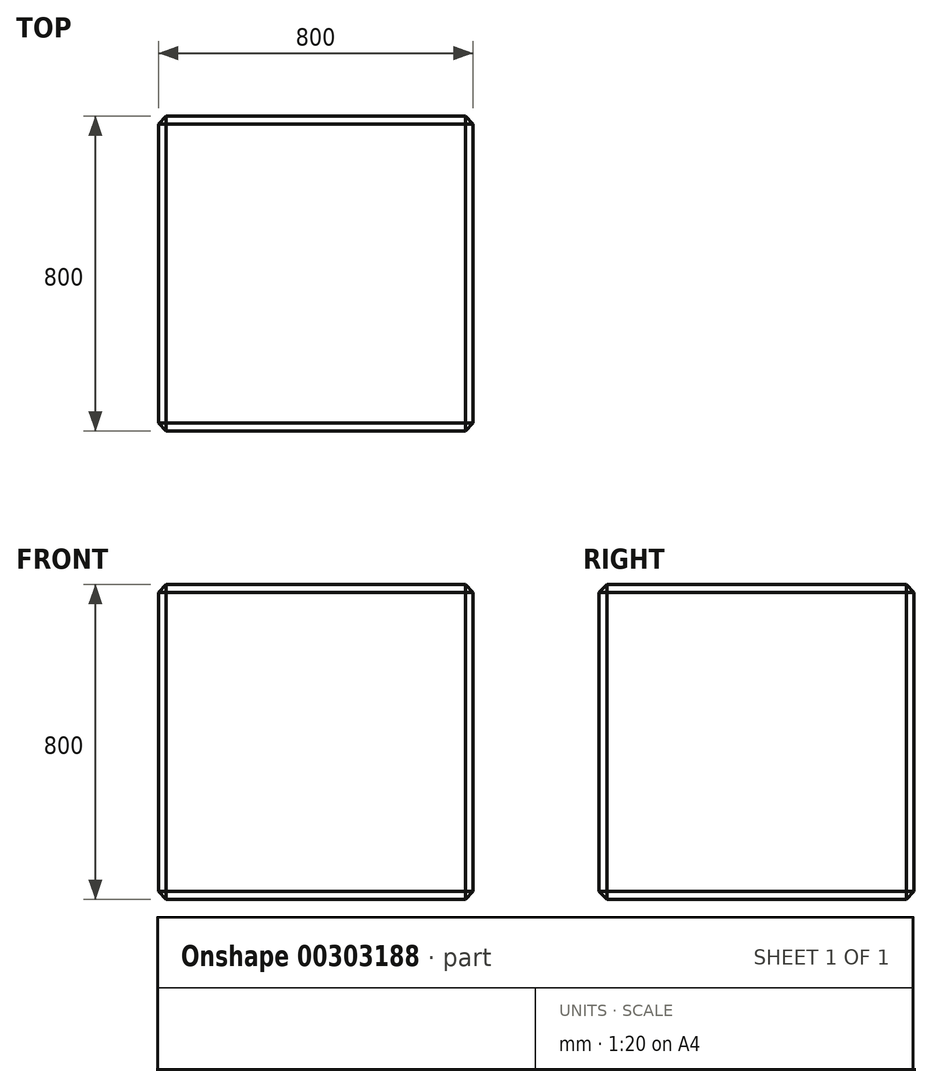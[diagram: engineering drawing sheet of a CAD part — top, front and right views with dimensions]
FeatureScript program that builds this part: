
annotation { "Feature Type Name" : "Feature", "Feature Type Description" : "" }
export const myFeature = defineFeature(function(context is Context, id is Id, definition is map)
    precondition{}
    {
        {
            var Q0;
            Q0=qCreatedBy(makeId("Top.planeOp"),FACE);
            var sketch = newSketch(context, id + "F0", { "sketchPlane" : qUnion([Q0])});
            skLineSegment(sketch, "E0.bottom", {"start": v(-398.92, 387.82) * mm, "end": v(401.08, 387.82) * mm});
            skLineSegment(sketch, "E0.top", {"start": v(-398.92, -412.18) * mm, "end": v(401.08, -412.18) * mm});
            skLineSegment(sketch, "E0.left", {"start": v(-398.92, 387.82) * mm, "end": v(-398.92, -412.18) * mm});
            skLineSegment(sketch, "E0.right", {"start": v(401.08, 387.82) * mm, "end": v(401.08, -412.18) * mm});
            skSolve(sketch);
        }
        {
            var Q0;
            Q0=makeQuery(id+"F0.imprint","IMPRINT",FACE,{"disambiguationData":[TD([[makeQuery(id+"F0.imprint","IMPRINT",EDGE,{"derivedFrom":sQuery(id+"F0.wireOp",EDGE,"E0.bottom")}),-1.0]])]});
            extrude(context, id + "F1", {"entities" : qUnion([Q0]), "depth" : 800 * mm});
        }
        {
            var Q0;
            Q0=makeQuery(id+"F1.opExtrude","CAP_FACE",FACE,{"disambiguationData":[OSD([sQuery(id+"F0.wireOp",EDGE,"E0.bottom"),sQuery(id+"F0.wireOp",EDGE,"E0.top"),sQuery(id+"F0.wireOp",EDGE,"E0.left"),sQuery(id+"F0.wireOp",EDGE,"E0.right")])],"isStart":false});
            var Q1;
            Q1=makeQuery(id+"F1.opExtrude","SWEPT_FACE",FACE,{"disambiguationData":[OSD([sQuery(id+"F0.wireOp",EDGE,"E0.right")])]});
            var Q2;
            Q2=makeQuery(id+"F1.opExtrude","SWEPT_FACE",FACE,{"disambiguationData":[OSD([sQuery(id+"F0.wireOp",EDGE,"E0.left")])]});
            var Q3;
            Q3=makeQuery(id+"F1.opExtrude","CAP_FACE",FACE,{"disambiguationData":[OSD([sQuery(id+"F0.wireOp",EDGE,"E0.bottom"),sQuery(id+"F0.wireOp",EDGE,"E0.top"),sQuery(id+"F0.wireOp",EDGE,"E0.left"),sQuery(id+"F0.wireOp",EDGE,"E0.right")])],"isStart":true});
            var Q4;
            Q4=makeQuery(id+"F1.opExtrude","SWEPT_FACE",FACE,{"disambiguationData":[OSD([sQuery(id+"F0.wireOp",EDGE,"E0.top")])]});
            chamfer(context, id + "F2", {"entities" : qUnion([Q0, Q1, Q2, Q3, Q4]), "width" : 20 * mm, "tangentPropagation" : true});
        }
    });
